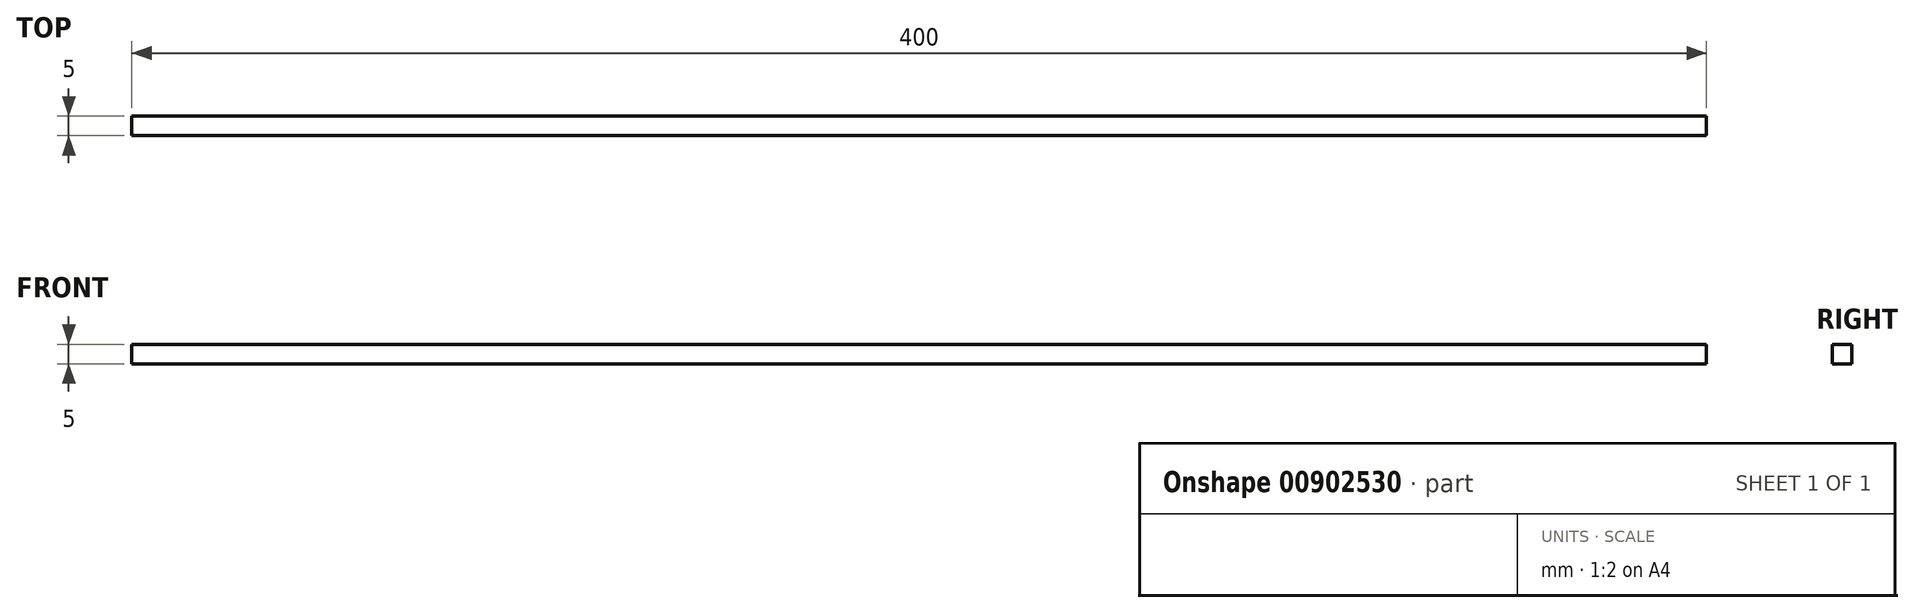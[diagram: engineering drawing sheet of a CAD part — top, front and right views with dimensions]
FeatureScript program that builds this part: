
annotation { "Feature Type Name" : "Feature", "Feature Type Description" : "" }
export const myFeature = defineFeature(function(context is Context, id is Id, definition is map)
    precondition{}
    {
        {
            var Q0;
            Q0=qCreatedBy(makeId("Right.planeOp"),FACE);
            var sketch = newSketch(context, id + "F0", { "sketchPlane" : qUnion([Q0])});
            skLineSegment(sketch, "E0.bottom", {"start": v(2.5, -2.5) * mm, "end": v(-2.5, -2.5) * mm});
            skLineSegment(sketch, "E0.top", {"start": v(2.5, 2.5) * mm, "end": v(-2.5, 2.5) * mm});
            skLineSegment(sketch, "E0.left", {"start": v(2.5, -2.5) * mm, "end": v(2.5, 2.5) * mm});
            skLineSegment(sketch, "E0.right", {"start": v(-2.5, -2.5) * mm, "end": v(-2.5, 2.5) * mm});
            skPoint(sketch, "E0.middle", {"position": v(0, 0) * mm});
            skSolve(sketch);
        }
        {
            var Q0;
            Q0=makeQuery(id+"F0.imprint","IMPRINT",FACE,{"disambiguationData":[TD([[makeQuery(id+"F0.imprint","IMPRINT",EDGE,{"derivedFrom":sQuery(id+"F0.wireOp",EDGE,"E0.bottom")}),-1.0]])]});
            extrude(context, id + "F1", {"entities" : qUnion([Q0]), "endBound" : BoundingType.SYMMETRIC, "depth" : 400 * mm, "offsetDistance" : 25 * mm});
        }
    });
